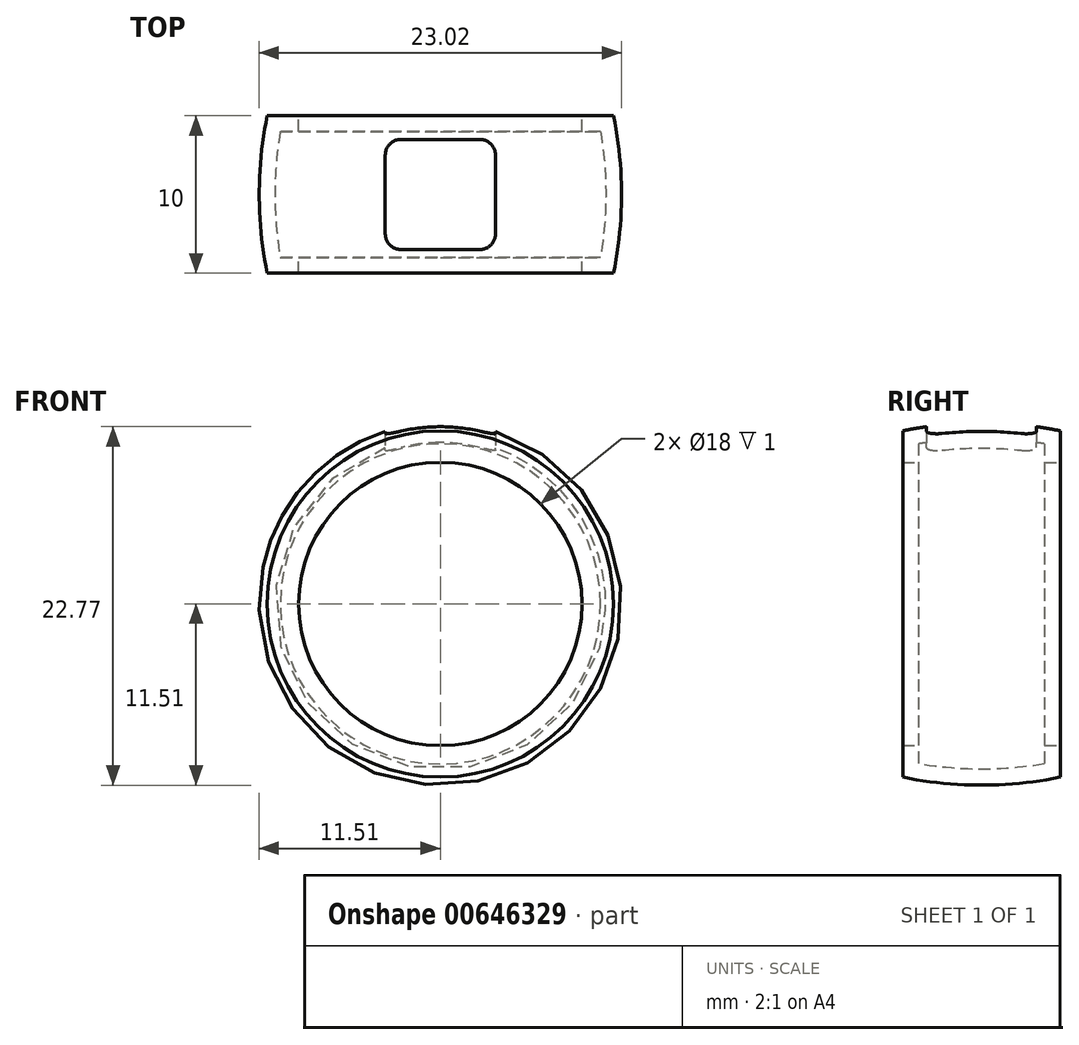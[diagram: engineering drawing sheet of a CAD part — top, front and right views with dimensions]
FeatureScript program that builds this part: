
annotation { "Feature Type Name" : "Feature", "Feature Type Description" : "" }
export const myFeature = defineFeature(function(context is Context, id is Id, definition is map)
    precondition{}
    {
        {
            var Q0;
            Q0=qCreatedBy(makeId("Top.planeOp"),FACE);
            var sketch = newSketch(context, id + "F0", { "sketchPlane" : qUnion([Q0])});
            skLineSegment(sketch, "E0", {"start": v(0, 0) * mm, "end": v(-9, 0) * mm, "construction": true});
            skLineSegment(sketch, "E1", {"start": v(-9, 5) * mm, "end": v(-9, -5) * mm});
            skLineSegment(sketch, "E2", {"start": v(-9, 5) * mm, "end": v(-11, 5) * mm});
            skLineSegment(sketch, "E3", {"start": v(-9, -5) * mm, "end": v(-11, -5) * mm});
            skArc(sketch, "E4", {"start": v(-11, 5) * mm, "mid": v(-11.5, 0) * mm, "end": v(-11, -5) * mm});
            skLineSegment(sketch, "E5", {"start": v(0, 0) * mm, "end": v(0, -18.96) * mm, "construction": true});
            skSolve(sketch);
        }
        {
            var Q0;
            Q0=makeQuery(id+"F0.imprint","IMPRINT",FACE,{"disambiguationData":[TD([[makeQuery(id+"F0.imprint","IMPRINT",EDGE,{"derivedFrom":sQuery(id+"F0.wireOp",EDGE,"E1")}),-1.0]])]});
            var Q1;
            Q1=sQuery(id+"F0.wireOp",EDGE,"E1");
            var Q2;
            Q2=sQuery(id+"F0.wireOp",EDGE,"E5");
            revolve(context, id + "F1", {"entities" : qUnion([Q0]), "surfaceEntities" : qUnion([Q1]), "axis" : qUnion([Q2]), "revolveType" : RevolveType.FULL});
        }
        {
            var Q0;
            Q0=makeQuery(id+"F1.opRevolve","SWEPT_FACE",FACE,{"disambiguationData":[OSD([sQuery(id+"F0.wireOp",EDGE,"E1")])]});
            shell(context, id + "F2", {"entities" : qUnion([Q0]), "thickness" : 1 * mm});
        }
        {
            var Q0;
            Q0=qCreatedBy(makeId("Top.planeOp"),FACE);
            var sketch = newSketch(context, id + "F3", { "sketchPlane" : qUnion([Q0])});
            skLineSegment(sketch, "E6.bottom", {"start": v(-2.5, 3.5) * mm, "end": v(2.5, 3.5) * mm});
            skLineSegment(sketch, "E6.top", {"start": v(-2.5, -3.5) * mm, "end": v(2.5, -3.5) * mm});
            skLineSegment(sketch, "E6.left", {"start": v(-3.5, 2.5) * mm, "end": v(-3.5, -2.5) * mm});
            skLineSegment(sketch, "E6.right", {"start": v(3.5, 2.5) * mm, "end": v(3.5, -2.5) * mm});
            skPoint(sketch, "E6.middle", {"position": v(0, 0) * mm});
            skLineSegment(sketch, "E7.bottom", {"start": v(0, -3.5) * mm, "end": v(0, -3.5) * mm});
            skLineSegment(sketch, "E7.top", {"start": v(0, -13.42) * mm, "end": v(0, -13.42) * mm});
            skLineSegment(sketch, "E7.left", {"start": v(0, -3.5) * mm, "end": v(0, -13.42) * mm});
            skLineSegment(sketch, "E7.right", {"start": v(0, -3.5) * mm, "end": v(0, -13.42) * mm});
            skPoint(sketch, "E7.middle", {"position": v(0, -8.46) * mm});
            skPoint(sketch, "E8.visualSharp", {"position": v(-3.5, 3.5) * mm});
            skArc(sketch, "E8.filletArc", {"start": v(-2.5, 3.5) * mm, "mid": v(-3.2, 3.2) * mm, "end": v(-3.5, 2.5) * mm});
            skPoint(sketch, "E9.visualSharp", {"position": v(3.5, 3.5) * mm});
            skArc(sketch, "E9.filletArc", {"start": v(3.5, 2.5) * mm, "mid": v(3.2, 3.2) * mm, "end": v(2.5, 3.5) * mm});
            skPoint(sketch, "E10.visualSharp", {"position": v(-3.5, -3.5) * mm});
            skArc(sketch, "E10.filletArc", {"start": v(-3.5, -2.5) * mm, "mid": v(-3.2, -3.2) * mm, "end": v(-2.5, -3.5) * mm});
            skPoint(sketch, "E11.visualSharp", {"position": v(3.5, -3.5) * mm});
            skArc(sketch, "E11.filletArc", {"start": v(2.5, -3.5) * mm, "mid": v(3.2, -3.2) * mm, "end": v(3.5, -2.5) * mm});
            skSolve(sketch);
        }
        {
            var Q0;
            Q0 = qSketchRegion(id + "F3", true);
            extrude(context, id + "F4", {"entities" : qUnion([Q0]), "operationType" : NewBodyOperationType.REMOVE, "endBound" : BoundingType.THROUGH_ALL, "depth" : 25 * mm, "offsetDistance" : 25 * mm});
        }
    });
